# Revit family: legrand boites de sol version ronde FR
name_source: partatom
category: Installations électriques
units: mm (PartAtom-declared; Revit-internal decimal feet)

## family parameters
Conserver l'orientation des annotations = Non
Cote de connecteur circulaire = Utiliser le diamètre
Couper avec des vides une fois chargée = Non
Hôte = Face
Partagée = Non
Point de calcul de pièce = Non
Type d'élément = Normal

## types (2) — shared parameters
Fabricant = LEGRAND
StdC125 = Type de sol utilisé : Plancher béton inférieur 125 mm
StdC170 = Type de sol utilisé : Plancher béton entre 125 mm et 170 mm
StdC250 = Type de sol utilisé : Plancher béton entre 170 mm et 250 mm
StdT = Type de sol utilisé : Plancher technique
Supports = 088127
Type du sol = Type de sol utilisé : Plancher béton inférieur 125 mm
zero-valued in all types: Elévation par défaut

## per-type parameters (varying)
| type | Description |
| 16 modules | Boite de sol ronde 16 modules vertical |
| 20 modules | Boite de sol ronde 20 modules horizontal |
